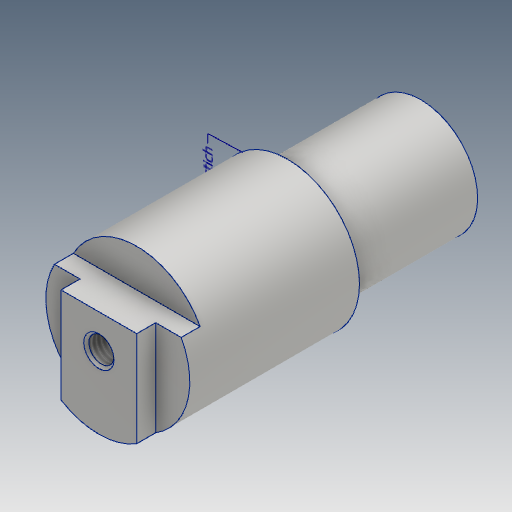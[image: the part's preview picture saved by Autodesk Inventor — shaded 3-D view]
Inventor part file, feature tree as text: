
AUTODESK INVENTOR PART (.ipt)
format: ipt  version: 2018.2 (Build 222227000, 227)  size: 195,584 bytes
history: native  units: mm
features: sketch x6, other x4, hole x2, extrude x2
ambient origin geometry x8: Origin, YZ Plane, XZ Plane, XY Plane, X Axis, Y Axis, Z Axis, Center Point
bodies: Volumenkörper1 (feature_tree)
feature tree (14):
  other  "200-10-ROCKER-BEARING-01.ipt"
  other  "Anmerkungen"
  other  "Grundkoerper"
  hole  "M6x12_CubeConn"  [1 undecoded]
  hole  "M6x12_BearingFix"  [1 undecoded]
  extrude  "Absatz_Torsionssicherung"  Depth=85.0mm
  extrude  "Absatz_Differential"  Depth=20.0mm
  sketch  "Skizze_Lagersitz"  dims[d91=4.917mm d92=12.0mm d93=6.0mm d94=2.0mm d95=90.0deg d96=17.1mm d97=20.594885mm d120=20.0mm d121=5.0mm d122=0.0mm d123=10.0mm d124=10.0mm d125=10.0mm d126=0.0mm d59=46.213283mm]
  sketch  "Skizze4"  dims[d1=10.0mm d3=30.2mm]
  sketch  "Skizze11"  dims[d4=5.0mm d5=30.0mm]
  sketch  "Skizze14"  dims[d6=38.0mm d7=85.0mm]
  sketch  "Skizze17"  dims[d10=90.0deg]
  sketch  "Skizze18"  dims[d69=6.647mm d70=16.0mm d71=8.0mm d72=2.0mm d73=90.0deg d74=25.0mm d75=20.594885mm]
  other  "Führungslinientext 1"
note: 2 required parameter values undecoded (feature->parameter linkage not recoverable at this tier; creation-order binding heuristic only, values carry confidence <= 0.55)
